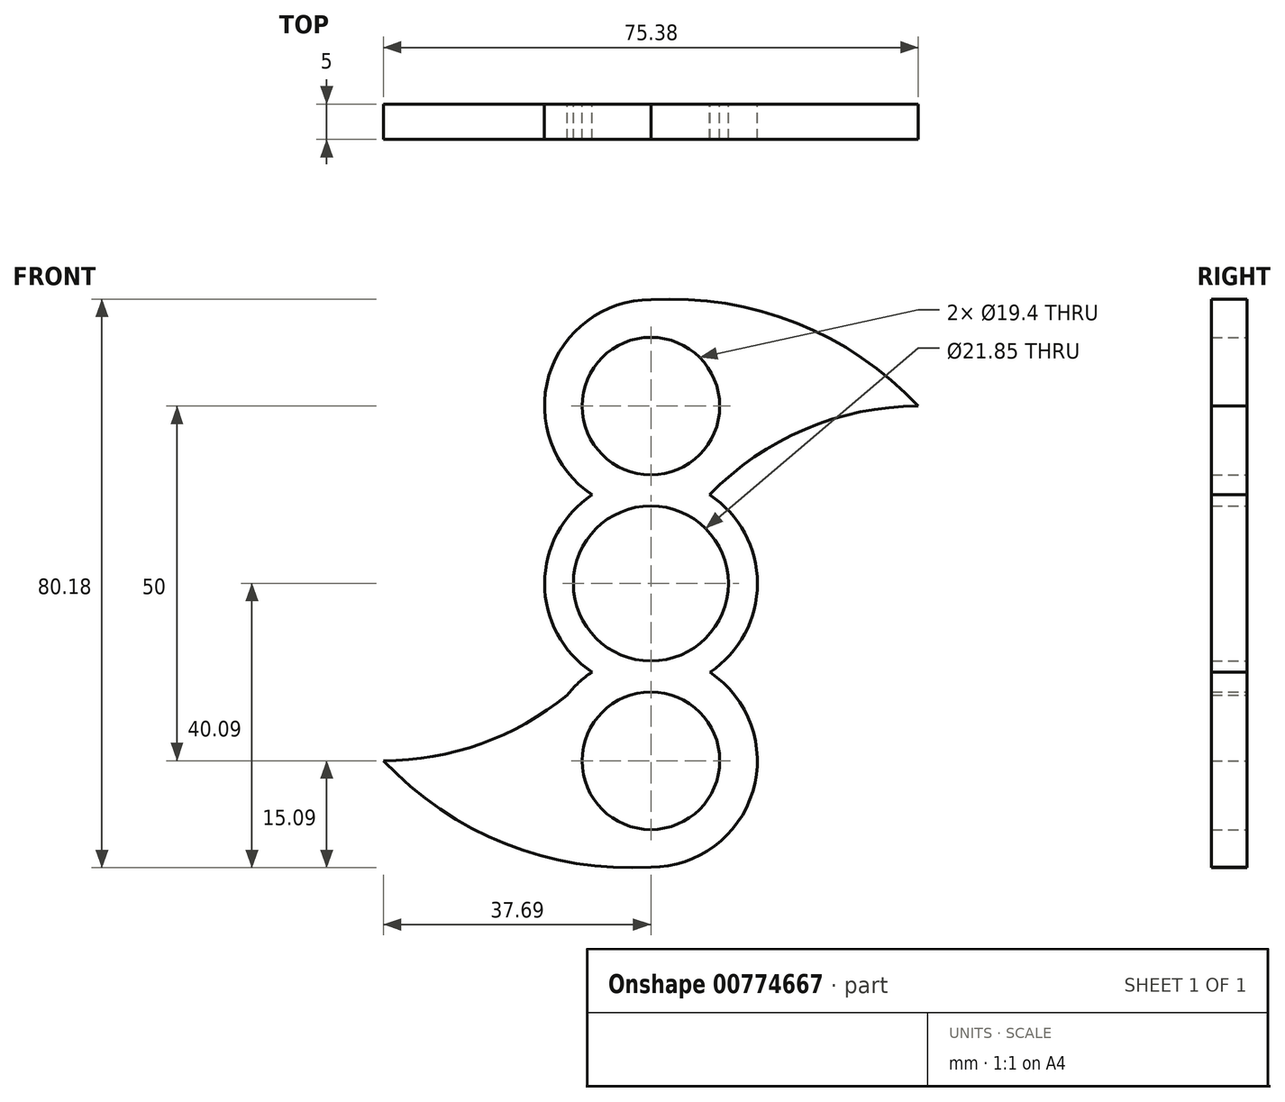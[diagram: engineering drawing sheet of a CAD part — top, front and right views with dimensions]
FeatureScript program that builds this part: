
annotation { "Feature Type Name" : "Feature", "Feature Type Description" : "" }
export const myFeature = defineFeature(function(context is Context, id is Id, definition is map)
    precondition{}
    {
        {
            var Q0;
            Q0=qCreatedBy(makeId("Front.planeOp"),FACE);
            var sketch = newSketch(context, id + "F0", { "sketchPlane" : qUnion([Q0])});
            skCircle(sketch, "E0", {"center": v(0, 0) * mm, "radius": 10.93 * mm});
            skLineSegment(sketch, "E1", {"start": v(0, 0) * mm, "end": v(0, 25) * mm, "construction": true});
            skCircle(sketch, "E2", {"center": v(0, 25) * mm, "radius": 9.7 * mm});
            skPoint(sketch, "E3.center", {"position": v(0.02, -0.02) * mm});
            skPoint(sketch, "E4.visualSharp", {"position": v(-22.84, 25.54) * mm});
            skPoint(sketch, "E5.visualSharp", {"position": v(22.28, -20.65) * mm});
            skArc(sketch, "E6", {"start": v(8.28, 12.5) * mm, "mid": v(10.18, 13.98) * mm, "end": v(11.8, 15.75) * mm});
            skPoint(sketch, "E7.orphan", {"position": v(0, 47.88) * mm});
            skPoint(sketch, "E8.end.orphan", {"position": v(0, -47.56) * mm});
            skArc(sketch, "E9.1.0", {"start": v(-8.3, -12.5) * mm, "mid": v(-10.18, -13.99) * mm, "end": v(-11.8, -15.75) * mm});
            skCircle(sketch, "E9.1.1", {"center": v(0, -25) * mm, "radius": 9.7 * mm});
            skArc(sketch, "E10", {"start": v(-8.27, 12.48) * mm, "mid": v(-14.98, 0) * mm, "end": v(-8.3, -12.5) * mm});
            skArc(sketch, "E11.trimOffspring", {"start": v(8.32, -12.52) * mm, "mid": v(15.02, 0) * mm, "end": v(8.28, 12.5) * mm});
            skLineSegment(sketch, "E12", {"start": v(0, 25) * mm, "end": v(37.69, 25) * mm, "construction": true});
            skArc(sketch, "E13", {"start": v(37.69, 25) * mm, "mid": v(20.51, 36.71) * mm, "end": v(0, 40) * mm});
            skPoint(sketch, "E13.endSnap0", {"position": v(0, 40) * mm});
            skArc(sketch, "E14", {"start": v(37.69, 25) * mm, "mid": v(21.71, 21.74) * mm, "end": v(8.28, 12.5) * mm});
            skLineSegment(sketch, "E15", {"start": v(0, -25) * mm, "end": v(-32.69, -25) * mm, "construction": true});
            skArc(sketch, "E16.1.0", {"start": v(-37.69, -25) * mm, "mid": v(-21.71, -21.74) * mm, "end": v(-8.28, -12.5) * mm});
            skArc(sketch, "E16.1.1", {"start": v(-37.69, -25) * mm, "mid": v(-20.51, -36.71) * mm, "end": v(0, -40) * mm});
            skArc(sketch, "E17.trimOffspring", {"start": v(0, 40) * mm, "mid": v(-14.37, 29.31) * mm, "end": v(-8.27, 12.48) * mm});
            skArc(sketch, "E18.trimOffspring", {"start": v(0, -40) * mm, "mid": v(14.36, -29.34) * mm, "end": v(8.32, -12.52) * mm});
            skSolve(sketch);
        }
        {
            var Q0;
            Q0=makeQuery(id+"F0.imprint","IMPRINT",FACE,{"disambiguationData":[TD([[makeQuery(id+"F0.imprint","IMPRINT",EDGE,{"derivedFrom":sQuery(id+"F0.wireOp",EDGE,"E0")}),-1.0]])]});
            extrude(context, id + "F1", {"entities" : qUnion([Q0]), "depth" : 5 * mm, "offsetDistance" : 25 * mm});
        }
    });
